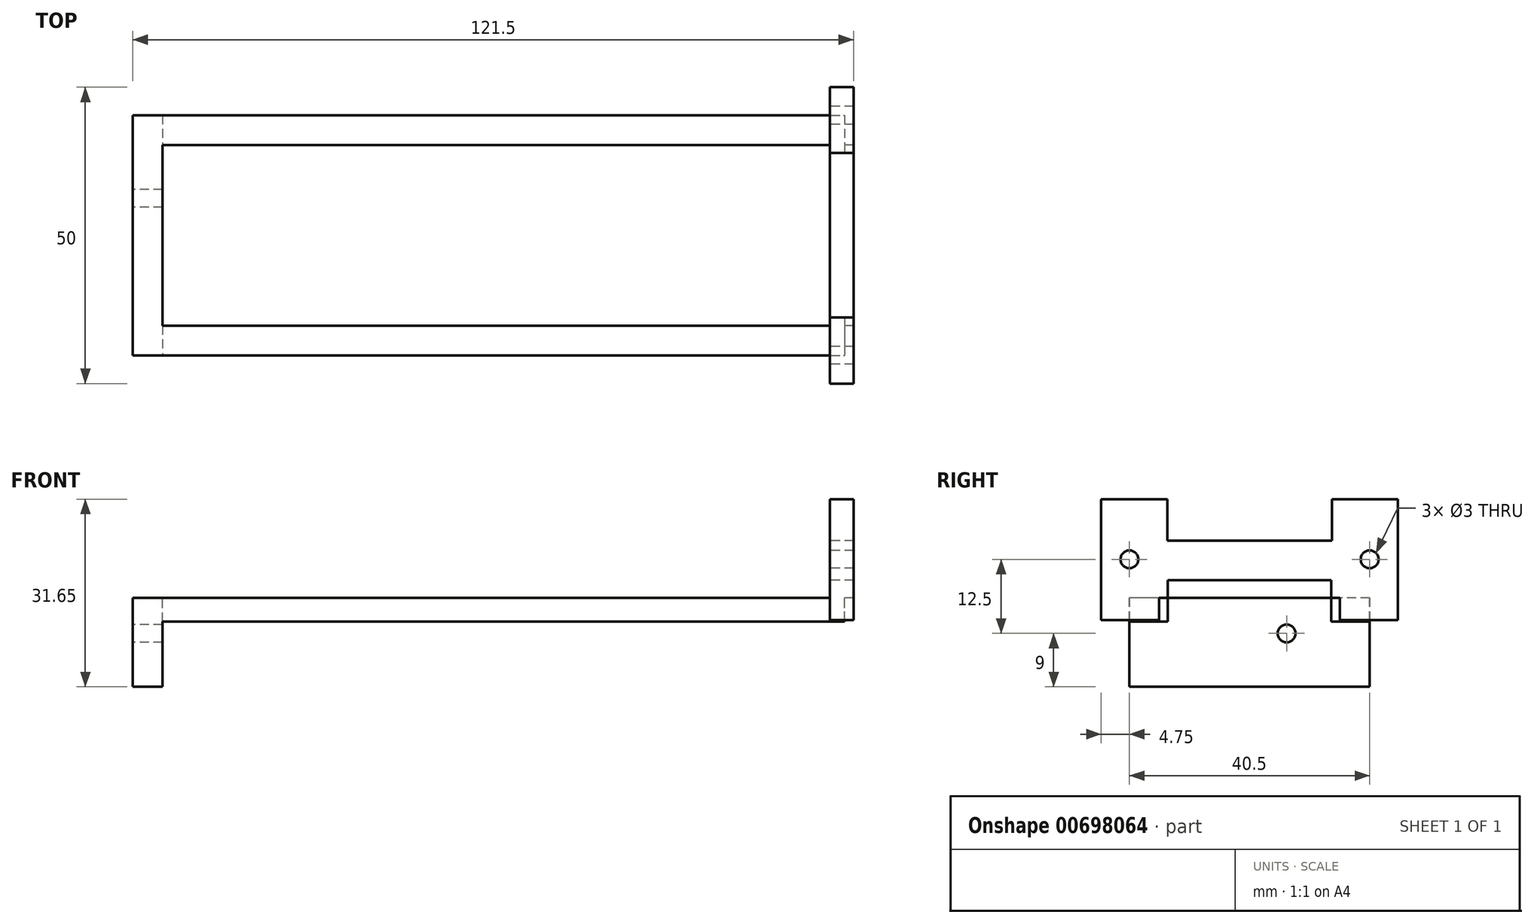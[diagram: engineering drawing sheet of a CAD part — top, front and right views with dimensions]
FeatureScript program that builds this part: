
annotation { "Feature Type Name" : "Feature", "Feature Type Description" : "" }
export const myFeature = defineFeature(function(context is Context, id is Id, definition is map)
    precondition{}
    {
        {
            var Q0;
            Q0=qCreatedBy(makeId("Top.planeOp"),FACE);
            var sketch = newSketch(context, id + "F0", { "sketchPlane" : qUnion([Q0])});
            skLineSegment(sketch, "E0.bottom", {"start": v(-60, 20.25) * mm, "end": v(60, 20.25) * mm});
            skLineSegment(sketch, "E0.top", {"start": v(-60, -20.25) * mm, "end": v(60, -20.25) * mm});
            skLineSegment(sketch, "E0.left", {"start": v(-60, 20.25) * mm, "end": v(-60, -20.25) * mm});
            skLineSegment(sketch, "E0.right", {"start": v(60, 20.25) * mm, "end": v(60, -20.25) * mm});
            skPoint(sketch, "E0.middle", {"position": v(0, 0) * mm});
            skLineSegment(sketch, "E1.bottom", {"start": v(-57.5, 15.25) * mm, "end": v(57.5, 15.25) * mm});
            skLineSegment(sketch, "E1.top", {"start": v(-57.5, -15.25) * mm, "end": v(57.5, -15.25) * mm});
            skLineSegment(sketch, "E1.left", {"start": v(-57.5, 15.25) * mm, "end": v(-57.5, -15.25) * mm});
            skLineSegment(sketch, "E1.right", {"start": v(57.5, 15.25) * mm, "end": v(57.5, -15.25) * mm});
            skSolve(sketch);
        }
        {
            var Q0;
            Q0 = qSketchRegion(id + "F0", true);
            extrude(context, id + "F1", {"entities" : qUnion([Q0]), "depth" : 4 * mm, "offsetDistance" : 25 * mm});
        }
        {
            var Q0;
            Q0=makeQuery(id+"F1.opExtrude","SWEPT_FACE",FACE,{"disambiguationData":[OSD([sQuery(id+"F0.wireOp",EDGE,"E0.left")])]});
            var sketch = newSketch(context, id + "F2", { "sketchPlane" : qUnion([Q0])});
            skLineSegment(sketch, "E2.bottom", {"start": v(20.25, 4) * mm, "end": v(-20.25, 4) * mm});
            skLineSegment(sketch, "E2.top", {"start": v(20.25, -11) * mm, "end": v(-20.25, -11) * mm});
            skLineSegment(sketch, "E2.left", {"start": v(20.25, 4) * mm, "end": v(20.25, -11) * mm});
            skLineSegment(sketch, "E2.right", {"start": v(-20.25, 4) * mm, "end": v(-20.25, -11) * mm});
            skLineSegment(sketch, "E3.bottom", {"start": v(-20.25, 4) * mm, "end": v(-6.25, 4) * mm, "construction": true});
            skLineSegment(sketch, "E3.top", {"start": v(-20.25, -2) * mm, "end": v(-6.25, -2) * mm, "construction": true});
            skLineSegment(sketch, "E3.left", {"start": v(-20.25, 4) * mm, "end": v(-20.25, -2) * mm, "construction": true});
            skLineSegment(sketch, "E3.right", {"start": v(-6.25, 4) * mm, "end": v(-6.25, -2) * mm, "construction": true});
            skCircle(sketch, "E4", {"center": v(-6.25, -2) * mm, "radius": 1.5 * mm});
            skSolve(sketch);
        }
        {
            var Q0;
            {var subQ3=sQuery(id+"F2.wireOp",EDGE,"E2.top");Q0=makeQuery(id+"F2.imprint","IMPRINT",FACE,{"disambiguationData":[TD([[makeQuery(id+"F2.imprint","IMPRINT",EDGE,{"derivedFrom":subQ3}),-1.0]])]});}
            var Q1;
            {var subQ6=sQuery(id+"F2.wireOp",EDGE,"E2.bottom");Q1=makeQuery(id+"F2.imprint","IMPRINT",FACE,{"disambiguationData":[TD([[makeQuery(id+"F2.imprint","IMPRINT",EDGE,{"derivedFrom":subQ6}),-1.0]])]});}
            extrude(context, id + "F3", {"entities" : qUnion([Q0, Q1]), "operationType" : NewBodyOperationType.ADD, "depth" : -5 * mm, "offsetDistance" : 25 * mm});
        }
        {
            var Q0;
            Q0=makeQuery(id+"F1.opExtrude","SWEPT_FACE",FACE,{"disambiguationData":[OSD([sQuery(id+"F0.wireOp",EDGE,"E1.right")])]});
            var sketch = newSketch(context, id + "F4", { "sketchPlane" : qUnion([Q0])});
            skLineSegment(sketch, "E5.bottom", {"start": v(25, 20.65) * mm, "end": v(-25, 20.65) * mm});
            skLineSegment(sketch, "E5.top", {"start": v(25, 0.23) * mm, "end": v(-25, 0.23) * mm});
            skLineSegment(sketch, "E5.left", {"start": v(25, 20.65) * mm, "end": v(25, 0.23) * mm});
            skLineSegment(sketch, "E5.right", {"start": v(-25, 20.65) * mm, "end": v(-25, 0.23) * mm});
            skPoint(sketch, "E5.middle", {"position": v(0, 10.44) * mm});
            skLineSegment(sketch, "E6.bottom", {"start": v(20.25, 10.5) * mm, "end": v(-20.25, 10.5) * mm, "construction": true});
            skLineSegment(sketch, "E6.top", {"start": v(20.25, -2.5) * mm, "end": v(-20.25, -2.5) * mm, "construction": true});
            skLineSegment(sketch, "E6.left", {"start": v(20.25, 10.5) * mm, "end": v(20.25, -2.5) * mm, "construction": true});
            skLineSegment(sketch, "E6.right", {"start": v(-20.25, 10.5) * mm, "end": v(-20.25, -2.5) * mm, "construction": true});
            skPoint(sketch, "E6.middle", {"position": v(0, 4) * mm});
            skCircle(sketch, "E7", {"center": v(20.25, 10.5) * mm, "radius": 1.5 * mm});
            skCircle(sketch, "E8", {"center": v(-20.25, 10.5) * mm, "radius": 1.5 * mm});
            skLineSegment(sketch, "E9.bottom", {"start": v(13.87, 13.65) * mm, "end": v(-13.87, 13.65) * mm});
            skLineSegment(sketch, "E9.top", {"start": v(13.87, 27.65) * mm, "end": v(-13.87, 27.65) * mm});
            skLineSegment(sketch, "E9.left", {"start": v(13.87, 13.65) * mm, "end": v(13.87, 27.65) * mm});
            skLineSegment(sketch, "E9.right", {"start": v(-13.87, 13.65) * mm, "end": v(-13.87, 27.65) * mm});
            skPoint(sketch, "E9.middle", {"position": v(0, 20.65) * mm});
            skLineSegment(sketch, "E10.bottom", {"start": v(13.77, 7) * mm, "end": v(-13.77, 7) * mm});
            skLineSegment(sketch, "E10.top", {"start": v(13.77, -7) * mm, "end": v(-13.77, -7) * mm});
            skLineSegment(sketch, "E10.left", {"start": v(13.77, 7) * mm, "end": v(13.77, -7) * mm});
            skLineSegment(sketch, "E10.right", {"start": v(-13.77, 7) * mm, "end": v(-13.77, -7) * mm});
            skPoint(sketch, "E10.middle", {"position": v(0, 0) * mm});
            skSolve(sketch);
        }
        {
            var Q0;
            Q0=makeQuery(id+"F4.imprint","IMPRINT",FACE,{"disambiguationData":[TD([[makeQuery(id+"F4.imprint","IMPRINT",EDGE,{"derivedFrom":sQuery(id+"F4.wireOp",EDGE,"E5.bottom")}),1.0]])]});
            extrude(context, id + "F5", {"entities" : qUnion([Q0]), "operationType" : NewBodyOperationType.ADD, "oppositeDirection" : true, "depth" : 4 * mm, "offsetDistance" : 25 * mm});
        }
        {
            var Q0;
            {var subQ0=sQuery(id+"F4.wireOp",EDGE,"E10.bottom");Q0=makeQuery(id+"F4.imprint","IMPRINT",FACE,{"disambiguationData":[TD([[makeQuery(id+"F4.imprint","IMPRINT",EDGE,{"derivedFrom":subQ0}),1.0]])]});}
            var Q1;
            {var subQ0=sQuery(id+"F4.wireOp",EDGE,"E10.left");var subQ1=sQuery(id+"F4.wireOp",EDGE,"E5.top");var subQ2=makeQuery(id+"F4.imprint","INTERSECT",VERTEX,{"derivedFrom":[subQ1,subQ0]});Q1=makeQuery(id+"F4.imprint","IMPRINT",FACE,{"disambiguationData":[TD([[makeQuery(id+"F4.imprint","IMPRINT",EDGE,{"disambiguationData":[TD([[subQ2,-1.0]])],"derivedFrom":subQ1}),1.0]])]});}
            var Q2;
            {var subQ0=sQuery(id+"F4.wireOp",EDGE,"E10.top");Q2=makeQuery(id+"F4.imprint","IMPRINT",FACE,{"disambiguationData":[TD([[makeQuery(id+"F4.imprint","IMPRINT",EDGE,{"derivedFrom":subQ0}),-1.0]])]});}
            var Q3;
            {var subQ0=sQuery(id+"F4.wireOp",EDGE,"E10.left");var subQ1=sQuery(id+"F4.wireOp",EDGE,"E5.top");var subQ2=makeQuery(id+"F4.imprint","INTERSECT",VERTEX,{"derivedFrom":[subQ1,subQ0]});Q3=makeQuery(id+"F4.imprint","IMPRINT",FACE,{"disambiguationData":[TD([[makeQuery(id+"F4.imprint","IMPRINT",EDGE,{"disambiguationData":[TD([[subQ2,-1.0]])],"derivedFrom":subQ1}),-1.0]])]});}
            extrude(context, id + "F6", {"entities" : qUnion([Q0, Q1, Q2, Q3]), "operationType" : NewBodyOperationType.REMOVE, "endBound" : BoundingType.THROUGH_ALL, "oppositeDirection" : true, "depth" : 25 * mm, "offsetDistance" : 25 * mm});
        }
    });
